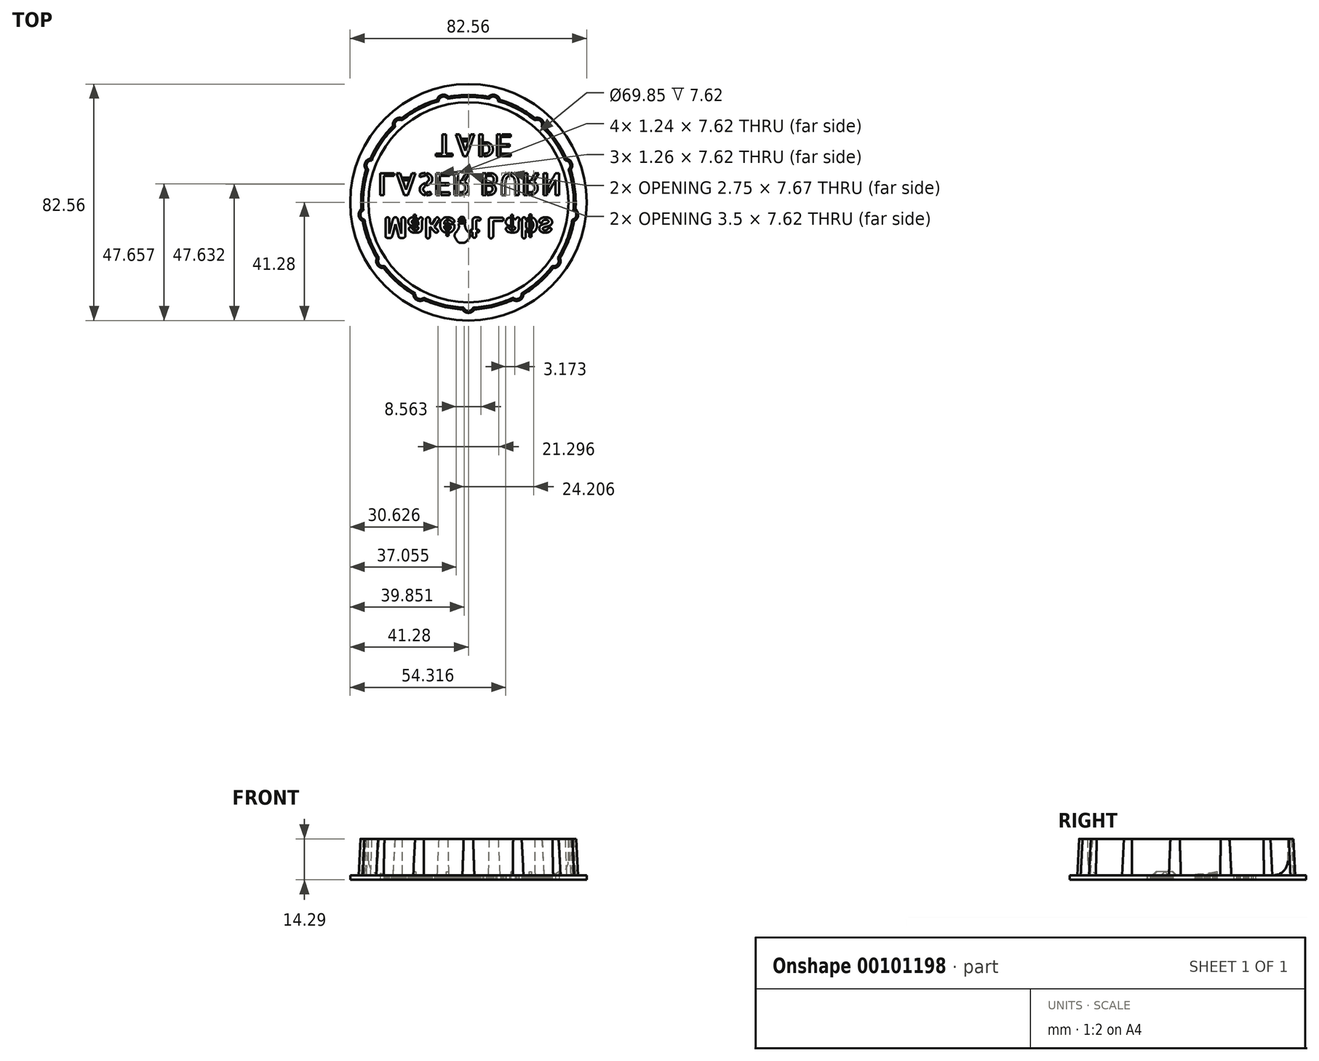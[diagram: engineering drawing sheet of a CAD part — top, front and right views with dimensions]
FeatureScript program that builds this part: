
annotation { "Feature Type Name" : "Feature", "Feature Type Description" : "" }
export const myFeature = defineFeature(function(context is Context, id is Id, definition is map)
    precondition{}
    {
        {
            var Q0;
            Q0=qCreatedBy(makeId("Top.planeOp"),FACE);
            var sketch = newSketch(context, id + "F0", { "sketchPlane" : qUnion([Q0])});
            skCircle(sketch, "E0", {"center": v(0, 0) * mm, "radius": 37.47 * mm});
            skArc(sketch, "E1", {"start": v(-2.08, -37.4) * mm, "mid": v(0, -38.6) * mm, "end": v(2.08, -37.4) * mm});
            skArc(sketch, "E2.1.0", {"start": v(15.54, -34.09) * mm, "mid": v(17.94, -34.19) * mm, "end": v(19.23, -32.16) * mm});
            skArc(sketch, "E2.2.0", {"start": v(29.6, -22.96) * mm, "mid": v(31.77, -21.93) * mm, "end": v(31.97, -19.54) * mm});
            skArc(sketch, "E2.3.0", {"start": v(36.88, -6.57) * mm, "mid": v(38.33, -4.65) * mm, "end": v(37.39, -2.44) * mm});
            skArc(sketch, "E2.4.0", {"start": v(35.71, 11.32) * mm, "mid": v(36.1, 13.7) * mm, "end": v(34.24, 15.2) * mm});
            skArc(sketch, "E2.5.0", {"start": v(26.36, 26.62) * mm, "mid": v(25.6, 28.9) * mm, "end": v(23.25, 29.38) * mm});
            skArc(sketch, "E2.6.0", {"start": v(10.97, 35.82) * mm, "mid": v(9.24, 37.49) * mm, "end": v(6.93, 36.82) * mm});
            skArc(sketch, "E2.7.0", {"start": v(-6.93, 36.82) * mm, "mid": v(-9.24, 37.49) * mm, "end": v(-10.97, 35.82) * mm});
            skArc(sketch, "E2.8.0", {"start": v(-23.25, 29.38) * mm, "mid": v(-25.6, 28.9) * mm, "end": v(-26.36, 26.62) * mm});
            skArc(sketch, "E2.9.0", {"start": v(-34.24, 15.2) * mm, "mid": v(-36.1, 13.7) * mm, "end": v(-35.71, 11.32) * mm});
            skArc(sketch, "E2.10.0", {"start": v(-37.39, -2.44) * mm, "mid": v(-38.33, -4.65) * mm, "end": v(-36.88, -6.57) * mm});
            skArc(sketch, "E2.11.0", {"start": v(-31.97, -19.54) * mm, "mid": v(-31.77, -21.93) * mm, "end": v(-29.6, -22.96) * mm});
            skArc(sketch, "E2.12.0", {"start": v(-19.23, -32.16) * mm, "mid": v(-17.94, -34.19) * mm, "end": v(-15.54, -34.09) * mm});
            skLineSegment(sketch, "E3", {"start": v(-2.08, -37.4) * mm, "end": v(0, -36.2) * mm});
            skLineSegment(sketch, "E4", {"start": v(0, -36.2) * mm, "end": v(2.08, -37.4) * mm});
            skSolve(sketch);
        }
        {
            var Q0;
            Q0 = qSketchRegion(id + "F0", true);
            extrude(context, id + "F1", {"entities" : qUnion([Q0]), "depth" : 12.7 * mm, "hasDraft" : true, "draftAngle" : 3 * degree, "draftPullDirection" : true});
        }
        {
            var Q0;
            Q0=qCreatedBy(makeId("Top.planeOp"),FACE);
            var sketch = newSketch(context, id + "F2", { "sketchPlane" : qUnion([Q0])});
            skCircle(sketch, "E5", {"center": v(0, 0) * mm, "radius": 38.1 * mm, "construction": true});
            skCircle(sketch, "E6", {"center": v(0, 0) * mm, "radius": 41.28 * mm});
            skSolve(sketch);
        }
        {
            var Q0;
            Q0 = qSketchRegion(id + "F2", true);
            extrude(context, id + "F3", {"entities" : qUnion([Q0]), "operationType" : NewBodyOperationType.ADD, "oppositeDirection" : true, "depth" : 1.59 * mm});
        }
        {
            var Q0;
            Q0=makeQuery(id+"F1.opExtrude","CAP_FACE",FACE,{"disambiguationData":[OSD([sQuery(id+"F0.wireOp",EDGE,"E0"),sQuery(id+"F0.wireOp",EDGE,"E1"),sQuery(id+"F0.wireOp",EDGE,"E2.1.0"),sQuery(id+"F0.wireOp",EDGE,"E2.2.0"),sQuery(id+"F0.wireOp",EDGE,"E2.3.0"),sQuery(id+"F0.wireOp",EDGE,"E2.4.0"),sQuery(id+"F0.wireOp",EDGE,"E2.5.0"),sQuery(id+"F0.wireOp",EDGE,"E2.6.0"),sQuery(id+"F0.wireOp",EDGE,"E2.7.0"),sQuery(id+"F0.wireOp",EDGE,"E2.8.0"),sQuery(id+"F0.wireOp",EDGE,"E2.9.0"),sQuery(id+"F0.wireOp",EDGE,"E2.10.0"),sQuery(id+"F0.wireOp",EDGE,"E2.11.0"),sQuery(id+"F0.wireOp",EDGE,"E2.12.0")])],"isStart":false});
            var sketch = newSketch(context, id + "F4", { "sketchPlane" : qUnion([Q0])});
            skCircle(sketch, "E7", {"center": v(0, 0) * mm, "radius": 34.93 * mm});
            skSolve(sketch);
        }
        {
            var Q0;
            Q0 = qSketchRegion(id + "F4", true);
            extrude(context, id + "F5", {"entities" : qUnion([Q0]), "operationType" : NewBodyOperationType.REMOVE, "oppositeDirection" : true, "depth" : 12.7 * mm});
        }
        {
            var Q0;
            Q0=makeQuery(id+"F5.boolean.opBoolean","COPY",EDGE,{"derivedFrom":makeQuery(id+"F5.opExtrude","CAP_EDGE",EDGE,{"disambiguationData":[OSD([sQuery(id+"F4.wireOp",EDGE,"E7")])],"isStart":false})});
            fillet(context, id + "F6", {"entities" : qUnion([Q0]), "radius" : 5.08 * mm, "tangentPropagation" : true, "allowEdgeOverflow" : false});
        }
        {
            var Q0;
            Q0=makeQuery(id+"F3.opExtrude","CAP_FACE",FACE,{"disambiguationData":[OSD([sQuery(id+"F2.wireOp",EDGE,"E6")])],"isStart":false});
            var sketch = newSketch(context, id + "F7", { "sketchPlane" : qUnion([Q0])});
            skFitSpline(sketch, "E8", {"points": [v(-27.6, 6.08) * mm, v(-27.6, 5.8) * mm, v(-27.65, 5.6) * mm, v(-27.77, 5.47) * mm]});
            skFitSpline(sketch, "E9", {"points": [v(-27.77, 5.47) * mm, v(-27.9, 5.34) * mm, v(-28.05, 5.27) * mm, v(-28.25, 5.27) * mm]});
            skFitSpline(sketch, "E10", {"points": [v(-28.25, 5.27) * mm, v(-28.44, 5.27) * mm, v(-28.6, 5.34) * mm, v(-28.72, 5.47) * mm]});
            skFitSpline(sketch, "E11", {"points": [v(-28.72, 5.47) * mm, v(-28.84, 5.6) * mm, v(-28.9, 5.8) * mm, v(-28.9, 6.08) * mm]});
            skLineSegment(sketch, "E12", {"start": v(-26.46, 6.45) * mm, "end": v(-27.6, 10.95) * mm});
            skLineSegment(sketch, "E13", {"start": v(-27.6, 10.95) * mm, "end": v(-27.6, 6.08) * mm});
            skFitSpline(sketch, "E14", {"points": [v(-28.9, 11.66) * mm, v(-28.9, 11.97) * mm, v(-28.83, 12.18) * mm, v(-28.66, 12.28) * mm]});
            skFitSpline(sketch, "E15", {"points": [v(-28.66, 12.28) * mm, v(-28.5, 12.4) * mm, v(-28.29, 12.45) * mm, v(-28.02, 12.45) * mm]});
            skLineSegment(sketch, "E16", {"start": v(-28.9, 6.08) * mm, "end": v(-28.9, 11.66) * mm});
            skLineSegment(sketch, "E17", {"start": v(-28.9, 11.66) * mm, "end": v(-28.9, 6.08) * mm});
            skFitSpline(sketch, "E18", {"points": [v(-27.57, 12.45) * mm, v(-27.3, 12.45) * mm, v(-27.11, 12.42) * mm, v(-27, 12.37) * mm]});
            skFitSpline(sketch, "E19", {"points": [v(-27, 12.37) * mm, v(-26.87, 12.33) * mm, v(-26.78, 12.24) * mm, v(-26.73, 12.11) * mm]});
            skFitSpline(sketch, "E20", {"points": [v(-26.73, 12.11) * mm, v(-26.67, 11.99) * mm, v(-26.6, 11.78) * mm, v(-26.53, 11.5) * mm]});
            skLineSegment(sketch, "E21", {"start": v(-28.02, 12.45) * mm, "end": v(-27.57, 12.45) * mm});
            skLineSegment(sketch, "E22", {"start": v(-27.57, 12.45) * mm, "end": v(-28.02, 12.45) * mm});
            skFitSpline(sketch, "E23", {"points": [v(-24.48, 11.5) * mm, v(-24.4, 11.78) * mm, v(-24.34, 11.99) * mm, v(-24.28, 12.11) * mm]});
            skFitSpline(sketch, "E24", {"points": [v(-24.28, 12.11) * mm, v(-24.22, 12.24) * mm, v(-24.13, 12.33) * mm, v(-24.01, 12.37) * mm]});
            skFitSpline(sketch, "E25", {"points": [v(-24.01, 12.37) * mm, v(-23.9, 12.42) * mm, v(-23.7, 12.45) * mm, v(-23.43, 12.45) * mm]});
            skLineSegment(sketch, "E26", {"start": v(-26.53, 11.5) * mm, "end": v(-25.5, 7.64) * mm});
            skLineSegment(sketch, "E27", {"start": v(-25.5, 7.64) * mm, "end": v(-24.48, 11.5) * mm});
            skFitSpline(sketch, "E28", {"points": [v(-23, 12.45) * mm, v(-22.72, 12.45) * mm, v(-22.5, 12.4) * mm, v(-22.34, 12.28) * mm]});
            skFitSpline(sketch, "E29", {"points": [v(-22.34, 12.28) * mm, v(-22.18, 12.18) * mm, v(-22.1, 11.97) * mm, v(-22.1, 11.66) * mm]});
            skLineSegment(sketch, "E30", {"start": v(-23.43, 12.45) * mm, "end": v(-23, 12.45) * mm});
            skLineSegment(sketch, "E31", {"start": v(-23, 12.45) * mm, "end": v(-23.43, 12.45) * mm});
            skFitSpline(sketch, "E32", {"points": [v(-22.1, 6.08) * mm, v(-22.1, 5.8) * mm, v(-22.16, 5.6) * mm, v(-22.28, 5.47) * mm]});
            skFitSpline(sketch, "E33", {"points": [v(-22.28, 5.47) * mm, v(-22.4, 5.34) * mm, v(-22.56, 5.27) * mm, v(-22.77, 5.27) * mm]});
            skFitSpline(sketch, "E34", {"points": [v(-22.77, 5.27) * mm, v(-22.95, 5.27) * mm, v(-23.11, 5.34) * mm, v(-23.23, 5.47) * mm]});
            skFitSpline(sketch, "E35", {"points": [v(-23.23, 5.47) * mm, v(-23.35, 5.6) * mm, v(-23.41, 5.8) * mm, v(-23.41, 6.08) * mm]});
            skLineSegment(sketch, "E36", {"start": v(-22.1, 11.66) * mm, "end": v(-22.1, 6.08) * mm});
            skLineSegment(sketch, "E37", {"start": v(-22.1, 6.08) * mm, "end": v(-22.1, 11.66) * mm});
            skFitSpline(sketch, "E38", {"points": [v(-24.55, 6.45) * mm, v(-24.62, 6.16) * mm, v(-24.68, 5.95) * mm, v(-24.73, 5.81) * mm]});
            skFitSpline(sketch, "E39", {"points": [v(-24.73, 5.81) * mm, v(-24.77, 5.68) * mm, v(-24.86, 5.55) * mm, v(-24.98, 5.44) * mm]});
            skFitSpline(sketch, "E40", {"points": [v(-24.98, 5.44) * mm, v(-25.1, 5.33) * mm, v(-25.28, 5.27) * mm, v(-25.5, 5.27) * mm]});
            skFitSpline(sketch, "E41", {"points": [v(-25.5, 5.27) * mm, v(-25.67, 5.27) * mm, v(-25.81, 5.3) * mm, v(-25.93, 5.38) * mm]});
            skFitSpline(sketch, "E42", {"points": [v(-25.93, 5.38) * mm, v(-26.04, 5.45) * mm, v(-26.13, 5.54) * mm, v(-26.2, 5.66) * mm]});
            skFitSpline(sketch, "E43", {"points": [v(-26.2, 5.66) * mm, v(-26.26, 5.77) * mm, v(-26.31, 5.9) * mm, v(-26.35, 6.03) * mm]});
            skFitSpline(sketch, "E44", {"points": [v(-26.35, 6.03) * mm, v(-26.38, 6.17) * mm, v(-26.42, 6.3) * mm, v(-26.46, 6.45) * mm]});
            skLineSegment(sketch, "E45", {"start": v(-23.41, 6.08) * mm, "end": v(-23.41, 10.95) * mm});
            skLineSegment(sketch, "E46", {"start": v(-23.41, 10.95) * mm, "end": v(-24.55, 6.45) * mm});
            skFitSpline(sketch, "E47", {"points": [v(-17.4, 6.01) * mm, v(-17.72, 5.76) * mm, v(-18.03, 5.58) * mm, v(-18.33, 5.46) * mm]});
            skFitSpline(sketch, "E48", {"points": [v(-18.33, 5.46) * mm, v(-18.62, 5.33) * mm, v(-18.96, 5.27) * mm, v(-19.32, 5.27) * mm]});
            skFitSpline(sketch, "E49", {"points": [v(-19.32, 5.27) * mm, v(-19.66, 5.27) * mm, v(-19.96, 5.34) * mm, v(-20.21, 5.47) * mm]});
            skFitSpline(sketch, "E50", {"points": [v(-20.21, 5.47) * mm, v(-20.47, 5.6) * mm, v(-20.66, 5.78) * mm, v(-20.8, 6.01) * mm]});
            skFitSpline(sketch, "E51", {"points": [v(-20.8, 6.01) * mm, v(-20.94, 6.24) * mm, v(-21, 6.49) * mm, v(-21, 6.75) * mm]});
            skFitSpline(sketch, "E52", {"points": [v(-21, 6.75) * mm, v(-21, 7.11) * mm, v(-20.9, 7.42) * mm, v(-20.67, 7.67) * mm]});
            skFitSpline(sketch, "E53", {"points": [v(-20.67, 7.67) * mm, v(-20.44, 7.93) * mm, v(-20.13, 8.1) * mm, v(-19.73, 8.18) * mm]});
            skFitSpline(sketch, "E54", {"points": [v(-19.73, 8.18) * mm, v(-19.65, 8.2) * mm, v(-19.44, 8.24) * mm, v(-19.1, 8.31) * mm]});
            skFitSpline(sketch, "E55", {"points": [v(-19.1, 8.31) * mm, v(-18.78, 8.38) * mm, v(-18.5, 8.44) * mm, v(-18.26, 8.5) * mm]});
            skFitSpline(sketch, "E56", {"points": [v(-18.26, 8.5) * mm, v(-18.02, 8.55) * mm, v(-17.77, 8.62) * mm, v(-17.5, 8.7) * mm]});
            skFitSpline(sketch, "E57", {"points": [v(-17.5, 8.7) * mm, v(-17.5, 9.05) * mm, v(-17.58, 9.3) * mm, v(-17.7, 9.46) * mm]});
            skFitSpline(sketch, "E58", {"points": [v(-17.7, 9.46) * mm, v(-17.82, 9.63) * mm, v(-18.08, 9.7) * mm, v(-18.47, 9.7) * mm]});
            skFitSpline(sketch, "E59", {"points": [v(-18.47, 9.7) * mm, v(-18.8, 9.7) * mm, v(-19.05, 9.66) * mm, v(-19.22, 9.57) * mm]});
            skFitSpline(sketch, "E60", {"points": [v(-19.22, 9.57) * mm, v(-19.39, 9.47) * mm, v(-19.53, 9.34) * mm, v(-19.65, 9.15) * mm]});
            skFitSpline(sketch, "E61", {"points": [v(-19.65, 9.15) * mm, v(-19.77, 8.96) * mm, v(-19.86, 8.84) * mm, v(-19.9, 8.78) * mm]});
            skFitSpline(sketch, "E62", {"points": [v(-19.9, 8.78) * mm, v(-19.96, 8.72) * mm, v(-20.07, 8.7) * mm, v(-20.23, 8.7) * mm]});
            skFitSpline(sketch, "E63", {"points": [v(-20.23, 8.7) * mm, v(-20.38, 8.7) * mm, v(-20.5, 8.74) * mm, v(-20.61, 8.83) * mm]});
            skFitSpline(sketch, "E64", {"points": [v(-20.61, 8.83) * mm, v(-20.72, 8.93) * mm, v(-20.77, 9.05) * mm, v(-20.77, 9.2) * mm]});
            skFitSpline(sketch, "E65", {"points": [v(-20.77, 9.2) * mm, v(-20.77, 9.43) * mm, v(-20.7, 9.65) * mm, v(-20.53, 9.87) * mm]});
            skFitSpline(sketch, "E66", {"points": [v(-20.53, 9.87) * mm, v(-20.36, 10.09) * mm, v(-20.1, 10.27) * mm, v(-19.76, 10.4) * mm]});
            skFitSpline(sketch, "E67", {"points": [v(-19.76, 10.4) * mm, v(-19.42, 10.55) * mm, v(-18.98, 10.62) * mm, v(-18.47, 10.62) * mm]});
            skFitSpline(sketch, "E68", {"points": [v(-18.47, 10.62) * mm, v(-17.9, 10.62) * mm, v(-17.44, 10.55) * mm, v(-17.1, 10.42) * mm]});
            skFitSpline(sketch, "E69", {"points": [v(-17.1, 10.42) * mm, v(-16.78, 10.28) * mm, v(-16.54, 10.07) * mm, v(-16.4, 9.77) * mm]});
            skFitSpline(sketch, "E70", {"points": [v(-16.4, 9.77) * mm, v(-16.27, 9.47) * mm, v(-16.2, 9.08) * mm, v(-16.2, 8.6) * mm]});
            skFitSpline(sketch, "E71", {"points": [v(-16.2, 8.6) * mm, v(-16.2, 8.29) * mm, v(-16.2, 8.03) * mm, v(-16.2, 7.81) * mm]});
            skFitSpline(sketch, "E72", {"points": [v(-16.2, 7.81) * mm, v(-16.2, 7.6) * mm, v(-16.2, 7.36) * mm, v(-16.21, 7.1) * mm]});
            skFitSpline(sketch, "E73", {"points": [v(-16.21, 7.1) * mm, v(-16.21, 6.85) * mm, v(-16.17, 6.6) * mm, v(-16.09, 6.32) * mm]});
            skFitSpline(sketch, "E74", {"points": [v(-16.09, 6.32) * mm, v(-16, 6.05) * mm, v(-15.97, 5.88) * mm, v(-15.97, 5.8) * mm]});
            skFitSpline(sketch, "E75", {"points": [v(-15.97, 5.8) * mm, v(-15.97, 5.67) * mm, v(-16.03, 5.55) * mm, v(-16.16, 5.44) * mm]});
            skFitSpline(sketch, "E76", {"points": [v(-16.16, 5.44) * mm, v(-16.28, 5.33) * mm, v(-16.43, 5.27) * mm, v(-16.59, 5.27) * mm]});
            skFitSpline(sketch, "E77", {"points": [v(-16.59, 5.27) * mm, v(-16.72, 5.27) * mm, v(-16.85, 5.33) * mm, v(-16.99, 5.46) * mm]});
            skFitSpline(sketch, "E78", {"points": [v(-16.99, 5.46) * mm, v(-17.12, 5.59) * mm, v(-17.26, 5.77) * mm, v(-17.4, 6.01) * mm]});
            skFitSpline(sketch, "E79", {"points": [v(-17.5, 7.91) * mm, v(-17.68, 7.84) * mm, v(-17.96, 7.77) * mm, v(-18.33, 7.69) * mm]});
            skFitSpline(sketch, "E80", {"points": [v(-18.33, 7.69) * mm, v(-18.7, 7.61) * mm, v(-18.95, 7.55) * mm, v(-19.1, 7.52) * mm]});
            skFitSpline(sketch, "E81", {"points": [v(-19.1, 7.52) * mm, v(-19.23, 7.48) * mm, v(-19.37, 7.4) * mm, v(-19.5, 7.3) * mm]});
            skFitSpline(sketch, "E82", {"points": [v(-19.5, 7.3) * mm, v(-19.63, 7.2) * mm, v(-19.7, 7.04) * mm, v(-19.7, 6.85) * mm]});
            skFitSpline(sketch, "E83", {"points": [v(-19.7, 6.85) * mm, v(-19.7, 6.65) * mm, v(-19.62, 6.48) * mm, v(-19.46, 6.34) * mm]});
            skFitSpline(sketch, "E84", {"points": [v(-19.46, 6.34) * mm, v(-19.31, 6.2) * mm, v(-19.12, 6.13) * mm, v(-18.87, 6.13) * mm]});
            skFitSpline(sketch, "E85", {"points": [v(-18.87, 6.13) * mm, v(-18.61, 6.13) * mm, v(-18.37, 6.19) * mm, v(-18.15, 6.3) * mm]});
            skFitSpline(sketch, "E86", {"points": [v(-18.15, 6.3) * mm, v(-17.93, 6.42) * mm, v(-17.77, 6.56) * mm, v(-17.67, 6.74) * mm]});
            skFitSpline(sketch, "E87", {"points": [v(-17.67, 6.74) * mm, v(-17.55, 6.94) * mm, v(-17.5, 7.27) * mm, v(-17.5, 7.73) * mm]});
            skLineSegment(sketch, "E88", {"start": v(-17.5, 7.73) * mm, "end": v(-17.5, 7.91) * mm});
            skLineSegment(sketch, "E89", {"start": v(-17.5, 7.91) * mm, "end": v(-17.5, 7.91) * mm});
            skLineSegment(sketch, "E90", {"start": v(-17.5, 7.91) * mm, "end": v(-17.5, 7.73) * mm});
            skFitSpline(sketch, "E91", {"points": [v(-13.47, 6.06) * mm, v(-13.47, 5.8) * mm, v(-13.54, 5.61) * mm, v(-13.67, 5.48) * mm]});
            skFitSpline(sketch, "E92", {"points": [v(-13.67, 5.48) * mm, v(-13.8, 5.34) * mm, v(-13.95, 5.27) * mm, v(-14.13, 5.27) * mm]});
            skFitSpline(sketch, "E93", {"points": [v(-14.13, 5.27) * mm, v(-14.33, 5.27) * mm, v(-14.49, 5.34) * mm, v(-14.6, 5.47) * mm]});
            skFitSpline(sketch, "E94", {"points": [v(-14.6, 5.47) * mm, v(-14.72, 5.6) * mm, v(-14.78, 5.8) * mm, v(-14.78, 6.07) * mm]});
            skLineSegment(sketch, "E95", {"start": v(-11.6, 5.87) * mm, "end": v(-12.76, 7.78) * mm});
            skLineSegment(sketch, "E96", {"start": v(-12.76, 7.78) * mm, "end": v(-13.47, 7.1) * mm});
            skLineSegment(sketch, "E97", {"start": v(-13.47, 7.1) * mm, "end": v(-13.47, 6.06) * mm});
            skFitSpline(sketch, "E98", {"points": [v(-14.78, 11.67) * mm, v(-14.78, 11.96) * mm, v(-14.72, 12.18) * mm, v(-14.6, 12.34) * mm]});
            skFitSpline(sketch, "E99", {"points": [v(-14.6, 12.34) * mm, v(-14.5, 12.49) * mm, v(-14.34, 12.57) * mm, v(-14.13, 12.57) * mm]});
            skFitSpline(sketch, "E100", {"points": [v(-14.13, 12.57) * mm, v(-13.93, 12.57) * mm, v(-13.77, 12.5) * mm, v(-13.65, 12.36) * mm]});
            skFitSpline(sketch, "E101", {"points": [v(-13.65, 12.36) * mm, v(-13.53, 12.22) * mm, v(-13.47, 12.02) * mm, v(-13.47, 11.75) * mm]});
            skLineSegment(sketch, "E102", {"start": v(-14.78, 6.07) * mm, "end": v(-14.78, 11.67) * mm});
            skLineSegment(sketch, "E103", {"start": v(-14.78, 11.67) * mm, "end": v(-14.78, 6.07) * mm});
            skFitSpline(sketch, "E104", {"points": [v(-12, 10.11) * mm, v(-11.8, 10.3) * mm, v(-11.67, 10.44) * mm, v(-11.57, 10.5) * mm]});
            skFitSpline(sketch, "E105", {"points": [v(-11.57, 10.5) * mm, v(-11.48, 10.58) * mm, v(-11.36, 10.61) * mm, v(-11.22, 10.61) * mm]});
            skFitSpline(sketch, "E106", {"points": [v(-11.22, 10.61) * mm, v(-11.06, 10.61) * mm, v(-10.92, 10.56) * mm, v(-10.81, 10.46) * mm]});
            skFitSpline(sketch, "E107", {"points": [v(-10.81, 10.46) * mm, v(-10.7, 10.35) * mm, v(-10.65, 10.22) * mm, v(-10.65, 10.06) * mm]});
            skFitSpline(sketch, "E108", {"points": [v(-10.65, 10.06) * mm, v(-10.65, 9.87) * mm, v(-10.83, 9.61) * mm, v(-11.18, 9.3) * mm]});
            skLineSegment(sketch, "E109", {"start": v(-13.47, 11.75) * mm, "end": v(-13.47, 8.56) * mm});
            skLineSegment(sketch, "E110", {"start": v(-13.47, 8.56) * mm, "end": v(-12, 10.11) * mm});
            skFitSpline(sketch, "E111", {"points": [v(-10.53, 6.54) * mm, v(-10.43, 6.38) * mm, v(-10.36, 6.26) * mm, v(-10.32, 6.18) * mm]});
            skFitSpline(sketch, "E112", {"points": [v(-10.32, 6.18) * mm, v(-10.28, 6.1) * mm, v(-10.25, 6.02) * mm, v(-10.25, 5.94) * mm]});
            skFitSpline(sketch, "E113", {"points": [v(-10.25, 5.94) * mm, v(-10.25, 5.74) * mm, v(-10.31, 5.57) * mm, v(-10.42, 5.45) * mm]});
            skFitSpline(sketch, "E114", {"points": [v(-10.42, 5.45) * mm, v(-10.54, 5.33) * mm, v(-10.69, 5.27) * mm, v(-10.87, 5.27) * mm]});
            skFitSpline(sketch, "E115", {"points": [v(-10.87, 5.27) * mm, v(-11.04, 5.27) * mm, v(-11.16, 5.31) * mm, v(-11.25, 5.4) * mm]});
            skFitSpline(sketch, "E116", {"points": [v(-11.25, 5.4) * mm, v(-11.33, 5.49) * mm, v(-11.45, 5.64) * mm, v(-11.6, 5.87) * mm]});
            skLineSegment(sketch, "E117", {"start": v(-11.18, 9.3) * mm, "end": v(-11.88, 8.65) * mm});
            skLineSegment(sketch, "E118", {"start": v(-11.88, 8.65) * mm, "end": v(-10.53, 6.54) * mm});
            skFitSpline(sketch, "E119", {"points": [v(-8.5, 7.62) * mm, v(-8.5, 7.32) * mm, v(-8.43, 7.06) * mm, v(-8.32, 6.83) * mm]});
            skFitSpline(sketch, "E120", {"points": [v(-8.32, 6.83) * mm, v(-8.2, 6.6) * mm, v(-8.04, 6.43) * mm, v(-7.85, 6.32) * mm]});
            skFitSpline(sketch, "E121", {"points": [v(-7.85, 6.32) * mm, v(-7.66, 6.2) * mm, v(-7.44, 6.14) * mm, v(-7.2, 6.14) * mm]});
            skFitSpline(sketch, "E122", {"points": [v(-7.2, 6.14) * mm, v(-7.05, 6.14) * mm, v(-6.9, 6.16) * mm, v(-6.78, 6.2) * mm]});
            skFitSpline(sketch, "E123", {"points": [v(-6.78, 6.2) * mm, v(-6.65, 6.23) * mm, v(-6.52, 6.3) * mm, v(-6.4, 6.37) * mm]});
            skFitSpline(sketch, "E124", {"points": [v(-6.4, 6.37) * mm, v(-6.28, 6.45) * mm, v(-6.17, 6.53) * mm, v(-6.06, 6.62) * mm]});
            skFitSpline(sketch, "E125", {"points": [v(-6.06, 6.62) * mm, v(-5.96, 6.71) * mm, v(-5.83, 6.83) * mm, v(-5.66, 6.99) * mm]});
            skFitSpline(sketch, "E126", {"points": [v(-5.66, 6.99) * mm, v(-5.6, 7.05) * mm, v(-5.5, 7.08) * mm, v(-5.38, 7.08) * mm]});
            skFitSpline(sketch, "E127", {"points": [v(-5.38, 7.08) * mm, v(-5.24, 7.08) * mm, v(-5.13, 7.04) * mm, v(-5.05, 6.96) * mm]});
            skFitSpline(sketch, "E128", {"points": [v(-5.05, 6.96) * mm, v(-4.96, 6.9) * mm, v(-4.92, 6.79) * mm, v(-4.92, 6.65) * mm]});
            skFitSpline(sketch, "E129", {"points": [v(-4.92, 6.65) * mm, v(-4.92, 6.53) * mm, v(-4.97, 6.4) * mm, v(-5.06, 6.24) * mm]});
            skFitSpline(sketch, "E130", {"points": [v(-5.06, 6.24) * mm, v(-5.16, 6.08) * mm, v(-5.3, 5.92) * mm, v(-5.48, 5.78) * mm]});
            skFitSpline(sketch, "E131", {"points": [v(-5.48, 5.78) * mm, v(-5.67, 5.63) * mm, v(-5.9, 5.51) * mm, v(-6.2, 5.42) * mm]});
            skFitSpline(sketch, "E132", {"points": [v(-6.2, 5.42) * mm, v(-6.47, 5.32) * mm, v(-6.8, 5.27) * mm, v(-7.17, 5.27) * mm]});
            skFitSpline(sketch, "E133", {"points": [v(-7.17, 5.27) * mm, v(-8.01, 5.27) * mm, v(-8.67, 5.51) * mm, v(-9.14, 6) * mm]});
            skFitSpline(sketch, "E134", {"points": [v(-9.14, 6) * mm, v(-9.6, 6.47) * mm, v(-9.84, 7.13) * mm, v(-9.84, 7.95) * mm]});
            skFitSpline(sketch, "E135", {"points": [v(-9.84, 7.95) * mm, v(-9.84, 8.34) * mm, v(-9.78, 8.7) * mm, v(-9.67, 9.03) * mm]});
            skFitSpline(sketch, "E136", {"points": [v(-9.67, 9.03) * mm, v(-9.55, 9.36) * mm, v(-9.38, 9.65) * mm, v(-9.16, 9.89) * mm]});
            skFitSpline(sketch, "E137", {"points": [v(-9.16, 9.89) * mm, v(-8.94, 10.12) * mm, v(-8.67, 10.3) * mm, v(-8.34, 10.43) * mm]});
            skFitSpline(sketch, "E138", {"points": [v(-8.34, 10.43) * mm, v(-8.02, 10.56) * mm, v(-7.66, 10.62) * mm, v(-7.27, 10.62) * mm]});
            skFitSpline(sketch, "E139", {"points": [v(-7.27, 10.62) * mm, v(-6.75, 10.62) * mm, v(-6.31, 10.51) * mm, v(-5.95, 10.3) * mm]});
            skFitSpline(sketch, "E140", {"points": [v(-5.95, 10.3) * mm, v(-5.58, 10.08) * mm, v(-5.3, 9.8) * mm, v(-5.12, 9.46) * mm]});
            skFitSpline(sketch, "E141", {"points": [v(-5.12, 9.46) * mm, v(-4.94, 9.11) * mm, v(-4.85, 8.76) * mm, v(-4.85, 8.4) * mm]});
            skFitSpline(sketch, "E142", {"points": [v(-4.85, 8.4) * mm, v(-4.85, 8.08) * mm, v(-4.94, 7.86) * mm, v(-5.13, 7.77) * mm]});
            skFitSpline(sketch, "E143", {"points": [v(-5.13, 7.77) * mm, v(-5.32, 7.67) * mm, v(-5.59, 7.62) * mm, v(-5.93, 7.62) * mm]});
            skLineSegment(sketch, "E144", {"start": v(-5.93, 7.62) * mm, "end": v(-8.5, 7.62) * mm});
            skLineSegment(sketch, "E145", {"start": v(-8.5, 7.62) * mm, "end": v(-5.93, 7.62) * mm});
            skFitSpline(sketch, "E146", {"points": [v(-6.12, 8.37) * mm, v(-6.15, 8.81) * mm, v(-6.27, 9.15) * mm, v(-6.48, 9.37) * mm]});
            skFitSpline(sketch, "E147", {"points": [v(-6.48, 9.37) * mm, v(-6.69, 9.6) * mm, v(-6.97, 9.7) * mm, v(-7.3, 9.7) * mm]});
            skFitSpline(sketch, "E148", {"points": [v(-7.3, 9.7) * mm, v(-7.64, 9.7) * mm, v(-7.9, 9.6) * mm, v(-8.12, 9.37) * mm]});
            skFitSpline(sketch, "E149", {"points": [v(-8.12, 9.37) * mm, v(-8.33, 9.14) * mm, v(-8.45, 8.8) * mm, v(-8.5, 8.37) * mm]});
            skLineSegment(sketch, "E150", {"start": v(-8.5, 8.37) * mm, "end": v(-6.12, 8.37) * mm});
            skLineSegment(sketch, "E151", {"start": v(-6.12, 8.37) * mm, "end": v(-8.5, 8.37) * mm});
            skFitSpline(sketch, "E152", {"points": [v(1.4, 11.29) * mm, v(1.4, 11.5) * mm, v(1.41, 11.66) * mm, v(1.42, 11.78) * mm]});
            skFitSpline(sketch, "E153", {"points": [v(1.42, 11.78) * mm, v(1.43, 11.9) * mm, v(1.46, 12) * mm, v(1.52, 12.1) * mm]});
            skFitSpline(sketch, "E154", {"points": [v(1.52, 12.1) * mm, v(1.57, 12.18) * mm, v(1.64, 12.26) * mm, v(1.74, 12.31) * mm]});
            skFitSpline(sketch, "E155", {"points": [v(1.74, 12.31) * mm, v(1.83, 12.37) * mm, v(1.94, 12.4) * mm, v(2.06, 12.4) * mm]});
            skFitSpline(sketch, "E156", {"points": [v(2.06, 12.4) * mm, v(2.23, 12.4) * mm, v(2.38, 12.33) * mm, v(2.51, 12.2) * mm]});
            skFitSpline(sketch, "E157", {"points": [v(2.51, 12.2) * mm, v(2.6, 12.13) * mm, v(2.66, 12.02) * mm, v(2.68, 11.9) * mm]});
            skFitSpline(sketch, "E158", {"points": [v(2.68, 11.9) * mm, v(2.7, 11.78) * mm, v(2.72, 11.61) * mm, v(2.72, 11.4) * mm]});
            skLineSegment(sketch, "E159", {"start": v(1.26, 10.5) * mm, "end": v(1.4, 10.5) * mm});
            skLineSegment(sketch, "E160", {"start": v(1.4, 10.5) * mm, "end": v(1.4, 11.29) * mm});
            skFitSpline(sketch, "E161", {"points": [v(3.2, 10.5) * mm, v(3.39, 10.5) * mm, v(3.53, 10.45) * mm, v(3.63, 10.36) * mm]});
            skFitSpline(sketch, "E162", {"points": [v(3.63, 10.36) * mm, v(3.72, 10.28) * mm, v(3.77, 10.16) * mm, v(3.77, 10.03) * mm]});
            skFitSpline(sketch, "E163", {"points": [v(3.77, 10.03) * mm, v(3.77, 9.85) * mm, v(3.7, 9.73) * mm, v(3.56, 9.65) * mm]});
            skFitSpline(sketch, "E164", {"points": [v(3.56, 9.65) * mm, v(3.42, 9.58) * mm, v(3.22, 9.55) * mm, v(2.96, 9.55) * mm]});
            skLineSegment(sketch, "E165", {"start": v(2.72, 11.4) * mm, "end": v(2.72, 10.5) * mm});
            skLineSegment(sketch, "E166", {"start": v(2.72, 10.5) * mm, "end": v(3.2, 10.5) * mm});
            skFitSpline(sketch, "E167", {"points": [v(2.72, 7.13) * mm, v(2.72, 6.93) * mm, v(2.73, 6.77) * mm, v(2.74, 6.66) * mm]});
            skFitSpline(sketch, "E168", {"points": [v(2.74, 6.66) * mm, v(2.75, 6.55) * mm, v(2.8, 6.46) * mm, v(2.86, 6.39) * mm]});
            skFitSpline(sketch, "E169", {"points": [v(2.86, 6.39) * mm, v(2.92, 6.32) * mm, v(3.02, 6.29) * mm, v(3.16, 6.29) * mm]});
            skFitSpline(sketch, "E170", {"points": [v(3.16, 6.29) * mm, v(3.24, 6.29) * mm, v(3.34, 6.3) * mm, v(3.47, 6.33) * mm]});
            skFitSpline(sketch, "E171", {"points": [v(3.47, 6.33) * mm, v(3.6, 6.35) * mm, v(3.7, 6.37) * mm, v(3.78, 6.37) * mm]});
            skFitSpline(sketch, "E172", {"points": [v(3.78, 6.37) * mm, v(3.89, 6.37) * mm, v(3.98, 6.33) * mm, v(4.07, 6.24) * mm]});
            skFitSpline(sketch, "E173", {"points": [v(4.07, 6.24) * mm, v(4.15, 6.16) * mm, v(4.2, 6.05) * mm, v(4.2, 5.93) * mm]});
            skFitSpline(sketch, "E174", {"points": [v(4.2, 5.93) * mm, v(4.2, 5.71) * mm, v(4.08, 5.55) * mm, v(3.85, 5.44) * mm]});
            skFitSpline(sketch, "E175", {"points": [v(3.85, 5.44) * mm, v(3.62, 5.33) * mm, v(3.29, 5.27) * mm, v(2.85, 5.27) * mm]});
            skFitSpline(sketch, "E176", {"points": [v(2.85, 5.27) * mm, v(2.44, 5.27) * mm, v(2.13, 5.34) * mm, v(1.92, 5.48) * mm]});
            skFitSpline(sketch, "E177", {"points": [v(1.92, 5.48) * mm, v(1.7, 5.62) * mm, v(1.57, 5.8) * mm, v(1.5, 6.05) * mm]});
            skFitSpline(sketch, "E178", {"points": [v(1.5, 6.05) * mm, v(1.44, 6.3) * mm, v(1.4, 6.62) * mm, v(1.4, 7.03) * mm]});
            skLineSegment(sketch, "E179", {"start": v(2.96, 9.55) * mm, "end": v(2.72, 9.55) * mm});
            skLineSegment(sketch, "E180", {"start": v(2.72, 9.55) * mm, "end": v(2.72, 7.13) * mm});
            skFitSpline(sketch, "E181", {"points": [v(1.23, 9.55) * mm, v(1.04, 9.55) * mm, v(0.9, 9.6) * mm, v(0.8, 9.68) * mm]});
            skFitSpline(sketch, "E182", {"points": [v(0.8, 9.68) * mm, v(0.7, 9.77) * mm, v(0.65, 9.89) * mm, v(0.65, 10.03) * mm]});
            skFitSpline(sketch, "E183", {"points": [v(0.65, 10.03) * mm, v(0.65, 10.16) * mm, v(0.7, 10.28) * mm, v(0.8, 10.36) * mm]});
            skFitSpline(sketch, "E184", {"points": [v(0.8, 10.36) * mm, v(0.91, 10.45) * mm, v(1.06, 10.5) * mm, v(1.26, 10.5) * mm]});
            skLineSegment(sketch, "E185", {"start": v(1.4, 7.03) * mm, "end": v(1.4, 9.55) * mm});
            skLineSegment(sketch, "E186", {"start": v(1.4, 9.55) * mm, "end": v(1.23, 9.55) * mm});
            skFitSpline(sketch, "E187", {"points": [v(11.53, 6.57) * mm, v(11.76, 6.57) * mm, v(11.94, 6.5) * mm, v(12.06, 6.4) * mm]});
            skFitSpline(sketch, "E188", {"points": [v(12.06, 6.4) * mm, v(12.18, 6.28) * mm, v(12.25, 6.14) * mm, v(12.25, 5.97) * mm]});
            skFitSpline(sketch, "E189", {"points": [v(12.25, 5.97) * mm, v(12.25, 5.8) * mm, v(12.19, 5.66) * mm, v(12.06, 5.55) * mm]});
            skFitSpline(sketch, "E190", {"points": [v(12.06, 5.55) * mm, v(11.94, 5.44) * mm, v(11.76, 5.4) * mm, v(11.53, 5.4) * mm]});
            skLineSegment(sketch, "E191", {"start": v(8.63, 11.7) * mm, "end": v(8.63, 6.57) * mm});
            skLineSegment(sketch, "E192", {"start": v(8.63, 6.57) * mm, "end": v(11.53, 6.57) * mm});
            skFitSpline(sketch, "E193", {"points": [v(8.08, 5.4) * mm, v(7.77, 5.4) * mm, v(7.54, 5.46) * mm, v(7.4, 5.6) * mm]});
            skFitSpline(sketch, "E194", {"points": [v(7.4, 5.6) * mm, v(7.27, 5.74) * mm, v(7.2, 5.96) * mm, v(7.2, 6.27) * mm]});
            skLineSegment(sketch, "E195", {"start": v(11.53, 5.4) * mm, "end": v(8.08, 5.4) * mm});
            skLineSegment(sketch, "E196", {"start": v(8.08, 5.4) * mm, "end": v(11.53, 5.4) * mm});
            skFitSpline(sketch, "E197", {"points": [v(7.2, 11.7) * mm, v(7.2, 11.99) * mm, v(7.27, 12.2) * mm, v(7.4, 12.35) * mm]});
            skFitSpline(sketch, "E198", {"points": [v(7.4, 12.35) * mm, v(7.53, 12.5) * mm, v(7.7, 12.57) * mm, v(7.91, 12.57) * mm]});
            skFitSpline(sketch, "E199", {"points": [v(7.91, 12.57) * mm, v(8.13, 12.57) * mm, v(8.3, 12.5) * mm, v(8.43, 12.35) * mm]});
            skFitSpline(sketch, "E200", {"points": [v(8.43, 12.35) * mm, v(8.57, 12.2) * mm, v(8.63, 12) * mm, v(8.63, 11.7) * mm]});
            skLineSegment(sketch, "E201", {"start": v(7.2, 6.27) * mm, "end": v(7.2, 11.7) * mm});
            skLineSegment(sketch, "E202", {"start": v(7.2, 11.7) * mm, "end": v(7.2, 6.27) * mm});
            skFitSpline(sketch, "E203", {"points": [v(14.47, 9.49) * mm, v(14.8, 9.56) * mm, v(15.08, 9.62) * mm, v(15.32, 9.68) * mm, v(14.47, 9.49) * mm]});
            skFitSpline(sketch, "E204", {"points": [v(16.33, 8.7) * mm, v(16.31, 9.05) * mm, v(16.24, 9.3) * mm, v(16.12, 9.46) * mm], "construction": true});
            skFitSpline(sketch, "E205", {"points": [v(16.12, 9.46) * mm, v(16, 9.63) * mm, v(15.74, 9.7) * mm, v(15.35, 9.7) * mm], "construction": true});
            skFitSpline(sketch, "E206", {"points": [v(15.35, 9.7) * mm, v(15.02, 9.7) * mm, v(14.77, 9.66) * mm, v(14.6, 9.57) * mm], "construction": true});
            skFitSpline(sketch, "E207", {"points": [v(14.6, 9.57) * mm, v(14.43, 9.47) * mm, v(14.28, 9.34) * mm, v(14.16, 9.15) * mm], "construction": true});
            skFitSpline(sketch, "E208", {"points": [v(14.16, 9.15) * mm, v(14.04, 8.96) * mm, v(13.96, 8.84) * mm, v(13.9, 8.78) * mm], "construction": true});
            skFitSpline(sketch, "E209", {"points": [v(13.9, 8.78) * mm, v(13.86, 8.72) * mm, v(13.75, 8.7) * mm, v(13.59, 8.7) * mm], "construction": true});
            skFitSpline(sketch, "E210", {"points": [v(13.59, 8.7) * mm, v(13.44, 8.7) * mm, v(13.31, 8.74) * mm, v(13.2, 8.83) * mm], "construction": true});
            skFitSpline(sketch, "E211", {"points": [v(13.2, 8.83) * mm, v(13.1, 8.93) * mm, v(13.04, 9.05) * mm, v(13.04, 9.2) * mm, v(13.2, 8.83) * mm]});
            skFitSpline(sketch, "E212", {"points": [v(13.04, 9.2) * mm, v(13.04, 9.43) * mm, v(13.13, 9.65) * mm, v(13.3, 9.87) * mm], "construction": true});
            skFitSpline(sketch, "E213", {"points": [v(13.3, 9.87) * mm, v(13.45, 10.09) * mm, v(13.7, 10.27) * mm, v(14.06, 10.4) * mm], "construction": true});
            skFitSpline(sketch, "E214", {"points": [v(14.06, 10.4) * mm, v(14.4, 10.55) * mm, v(14.83, 10.62) * mm, v(15.35, 10.62) * mm], "construction": true});
            skFitSpline(sketch, "E215", {"points": [v(15.35, 10.62) * mm, v(15.93, 10.62) * mm, v(16.38, 10.55) * mm, v(16.71, 10.42) * mm], "construction": true});
            skFitSpline(sketch, "E216", {"points": [v(16.71, 10.42) * mm, v(17.04, 10.28) * mm, v(17.28, 10.07) * mm, v(17.41, 9.77) * mm], "construction": true});
            skFitSpline(sketch, "E217", {"points": [v(17.41, 9.77) * mm, v(17.55, 9.47) * mm, v(17.62, 9.08) * mm, v(17.62, 8.6) * mm], "construction": true});
            skFitSpline(sketch, "E218", {"points": [v(17.62, 8.6) * mm, v(17.62, 8.29) * mm, v(17.62, 8.03) * mm, v(17.61, 7.81) * mm], "construction": true});
            skFitSpline(sketch, "E219", {"points": [v(17.61, 7.81) * mm, v(17.61, 7.6) * mm, v(17.6, 7.36) * mm, v(17.6, 7.1) * mm], "construction": true});
            skFitSpline(sketch, "E220", {"points": [v(17.6, 7.1) * mm, v(17.6, 6.85) * mm, v(17.65, 6.6) * mm, v(17.73, 6.32) * mm], "construction": true});
            skFitSpline(sketch, "E221", {"points": [v(17.73, 6.32) * mm, v(17.81, 6.05) * mm, v(17.85, 5.88) * mm, v(17.85, 5.8) * mm], "construction": true});
            skFitSpline(sketch, "E222", {"points": [v(17.85, 5.8) * mm, v(17.85, 5.67) * mm, v(17.79, 5.55) * mm, v(17.66, 5.44) * mm], "construction": true});
            skFitSpline(sketch, "E223", {"points": [v(17.66, 5.44) * mm, v(17.54, 5.33) * mm, v(17.4, 5.27) * mm, v(17.23, 5.27) * mm], "construction": true});
            skFitSpline(sketch, "E224", {"points": [v(17.23, 5.27) * mm, v(17.1, 5.27) * mm, v(16.96, 5.33) * mm, v(16.83, 5.46) * mm], "construction": true});
            skFitSpline(sketch, "E225", {"points": [v(16.83, 5.46) * mm, v(16.7, 5.59) * mm, v(16.56, 5.77) * mm, v(16.41, 6.01) * mm, v(16.83, 5.46) * mm]});
            skFitSpline(sketch, "E226", {"points": [v(16.33, 7.91) * mm, v(16.13, 7.84) * mm, v(15.85, 7.77) * mm, v(15.49, 7.69) * mm]});
            skFitSpline(sketch, "E227", {"points": [v(15.53, 7.7) * mm, v(15.16, 7.62) * mm, v(14.9, 7.56) * mm, v(14.77, 7.52) * mm]});
            skFitSpline(sketch, "E228", {"points": [v(14.72, 7.52) * mm, v(14.58, 7.48) * mm, v(14.45, 7.4) * mm, v(14.32, 7.3) * mm]});
            skFitSpline(sketch, "E229", {"points": [v(14.32, 7.3) * mm, v(14.2, 7.2) * mm, v(14.13, 7.04) * mm, v(14.13, 6.85) * mm]});
            skFitSpline(sketch, "E230", {"points": [v(14.13, 6.85) * mm, v(14.13, 6.65) * mm, v(14.2, 6.48) * mm, v(14.35, 6.34) * mm]});
            skFitSpline(sketch, "E231", {"points": [v(14.35, 6.34) * mm, v(14.5, 6.2) * mm, v(14.7, 6.13) * mm, v(14.95, 6.13) * mm]});
            skFitSpline(sketch, "E232", {"points": [v(14.95, 6.13) * mm, v(15.2, 6.13) * mm, v(15.45, 6.19) * mm, v(15.67, 6.3) * mm]});
            skFitSpline(sketch, "E233", {"points": [v(15.67, 6.3) * mm, v(15.88, 6.42) * mm, v(16.05, 6.56) * mm, v(16.15, 6.74) * mm]});
            skFitSpline(sketch, "E234", {"points": [v(16.15, 6.74) * mm, v(16.27, 6.94) * mm, v(16.33, 7.27) * mm, v(16.33, 7.73) * mm]});
            skFitSpline(sketch, "E235", {"points": [v(20.03, 9.8) * mm, v(20.28, 10.07) * mm, v(20.53, 10.26) * mm, v(20.79, 10.4) * mm]});
            skFitSpline(sketch, "E236", {"points": [v(20.79, 10.4) * mm, v(21.04, 10.53) * mm, v(21.36, 10.6) * mm, v(21.74, 10.6) * mm]});
            skFitSpline(sketch, "E237", {"points": [v(21.74, 10.6) * mm, v(22.18, 10.6) * mm, v(22.56, 10.5) * mm, v(22.89, 10.3) * mm]});
            skFitSpline(sketch, "E238", {"points": [v(22.89, 10.3) * mm, v(23.22, 10.09) * mm, v(23.47, 9.79) * mm, v(23.65, 9.4) * mm]});
            skFitSpline(sketch, "E239", {"points": [v(23.65, 9.4) * mm, v(23.83, 9) * mm, v(23.92, 8.53) * mm, v(23.92, 8) * mm]});
            skFitSpline(sketch, "E240", {"points": [v(23.92, 8) * mm, v(23.92, 7.6) * mm, v(23.87, 7.23) * mm, v(23.77, 6.9) * mm]});
            skFitSpline(sketch, "E241", {"points": [v(23.77, 6.9) * mm, v(23.67, 6.57) * mm, v(23.53, 6.28) * mm, v(23.33, 6.04) * mm]});
            skFitSpline(sketch, "E242", {"points": [v(23.33, 6.04) * mm, v(23.14, 5.8) * mm, v(22.9, 5.6) * mm, v(22.63, 5.47) * mm]});
            skFitSpline(sketch, "E243", {"points": [v(22.63, 5.47) * mm, v(22.36, 5.34) * mm, v(22.06, 5.27) * mm, v(21.73, 5.27) * mm]});
            skFitSpline(sketch, "E244", {"points": [v(21.73, 5.27) * mm, v(21.52, 5.27) * mm, v(21.33, 5.3) * mm, v(21.16, 5.34) * mm]});
            skFitSpline(sketch, "E245", {"points": [v(21.16, 5.34) * mm, v(20.98, 5.4) * mm, v(20.83, 5.45) * mm, v(20.7, 5.53) * mm]});
            skFitSpline(sketch, "E246", {"points": [v(20.7, 5.53) * mm, v(20.58, 5.61) * mm, v(20.47, 5.7) * mm, v(20.38, 5.78) * mm]});
            skFitSpline(sketch, "E247", {"points": [v(20.38, 5.78) * mm, v(20.3, 5.86) * mm, v(20.18, 5.98) * mm, v(20.03, 6.15) * mm]});
            skLineSegment(sketch, "E248", {"start": v(20.03, 11.82) * mm, "end": v(20.03, 9.8) * mm});
            skLineSegment(sketch, "E249", {"start": v(20.03, 9.8) * mm, "end": v(20.03, 11.82) * mm});
            skFitSpline(sketch, "E250", {"points": [v(20.03, 6.02) * mm, v(20.03, 5.77) * mm, v(19.97, 5.59) * mm, v(19.85, 5.46) * mm]});
            skFitSpline(sketch, "E251", {"points": [v(19.85, 5.46) * mm, v(19.74, 5.33) * mm, v(19.58, 5.27) * mm, v(19.4, 5.27) * mm]});
            skFitSpline(sketch, "E252", {"points": [v(19.4, 5.27) * mm, v(19.22, 5.27) * mm, v(19.07, 5.33) * mm, v(18.96, 5.46) * mm]});
            skFitSpline(sketch, "E253", {"points": [v(18.96, 5.46) * mm, v(18.85, 5.59) * mm, v(18.8, 5.77) * mm, v(18.8, 6.02) * mm]});
            skLineSegment(sketch, "E254", {"start": v(20.03, 6.15) * mm, "end": v(20.03, 6.02) * mm});
            skLineSegment(sketch, "E255", {"start": v(20.03, 6.02) * mm, "end": v(20.03, 6.15) * mm});
            skFitSpline(sketch, "E256", {"points": [v(18.8, 11.76) * mm, v(18.8, 12.02) * mm, v(18.84, 12.23) * mm, v(18.95, 12.36) * mm]});
            skFitSpline(sketch, "E257", {"points": [v(18.95, 12.36) * mm, v(19.06, 12.5) * mm, v(19.2, 12.57) * mm, v(19.4, 12.57) * mm]});
            skFitSpline(sketch, "E258", {"points": [v(19.4, 12.57) * mm, v(19.6, 12.57) * mm, v(19.76, 12.5) * mm, v(19.87, 12.37) * mm]});
            skFitSpline(sketch, "E259", {"points": [v(19.87, 12.37) * mm, v(19.98, 12.24) * mm, v(20.03, 12.06) * mm, v(20.03, 11.82) * mm]});
            skLineSegment(sketch, "E260", {"start": v(18.8, 6.02) * mm, "end": v(18.8, 11.76) * mm});
            skLineSegment(sketch, "E261", {"start": v(18.8, 11.76) * mm, "end": v(18.8, 6.02) * mm});
            skFitSpline(sketch, "E262", {"points": [v(20.1, 7.91) * mm, v(20.1, 7.39) * mm, v(20.21, 6.99) * mm, v(20.45, 6.7) * mm]});
            skFitSpline(sketch, "E263", {"points": [v(20.45, 6.7) * mm, v(20.7, 6.43) * mm, v(21, 6.29) * mm, v(21.4, 6.29) * mm]});
            skFitSpline(sketch, "E264", {"points": [v(21.4, 6.29) * mm, v(21.72, 6.29) * mm, v(22, 6.43) * mm, v(22.25, 6.72) * mm]});
            skFitSpline(sketch, "E265", {"points": [v(22.25, 6.72) * mm, v(22.49, 7) * mm, v(22.6, 7.42) * mm, v(22.6, 7.95) * mm]});
            skFitSpline(sketch, "E266", {"points": [v(22.6, 7.95) * mm, v(22.6, 8.3) * mm, v(22.56, 8.6) * mm, v(22.46, 8.85) * mm]});
            skFitSpline(sketch, "E267", {"points": [v(22.46, 8.85) * mm, v(22.36, 9.1) * mm, v(22.22, 9.29) * mm, v(22.03, 9.43) * mm]});
            skFitSpline(sketch, "E268", {"points": [v(22.03, 9.43) * mm, v(21.85, 9.56) * mm, v(21.64, 9.63) * mm, v(21.4, 9.63) * mm]});
            skFitSpline(sketch, "E269", {"points": [v(21.4, 9.63) * mm, v(21.14, 9.63) * mm, v(20.92, 9.56) * mm, v(20.72, 9.43) * mm]});
            skFitSpline(sketch, "E270", {"points": [v(20.72, 9.43) * mm, v(20.53, 9.29) * mm, v(20.38, 9.1) * mm, v(20.26, 8.83) * mm]});
            skFitSpline(sketch, "E271", {"points": [v(20.26, 8.83) * mm, v(20.15, 8.58) * mm, v(20.1, 8.27) * mm, v(20.1, 7.91) * mm]});
            skFitSpline(sketch, "E272", {"points": [v(29.2, 6.99) * mm, v(29.2, 6.63) * mm, v(29.12, 6.32) * mm, v(28.94, 6.06) * mm]});
            skFitSpline(sketch, "E273", {"points": [v(28.94, 6.06) * mm, v(28.77, 5.8) * mm, v(28.5, 5.6) * mm, v(28.16, 5.47) * mm]});
            skFitSpline(sketch, "E274", {"points": [v(28.16, 5.47) * mm, v(27.82, 5.34) * mm, v(27.4, 5.27) * mm, v(26.9, 5.27) * mm]});
            skFitSpline(sketch, "E275", {"points": [v(26.9, 5.27) * mm, v(26.43, 5.27) * mm, v(26.03, 5.34) * mm, v(25.7, 5.49) * mm]});
            skFitSpline(sketch, "E276", {"points": [v(25.7, 5.49) * mm, v(25.35, 5.63) * mm, v(25.1, 5.81) * mm, v(24.94, 6.03) * mm]});
            skFitSpline(sketch, "E277", {"points": [v(24.94, 6.03) * mm, v(24.78, 6.25) * mm, v(24.7, 6.46) * mm, v(24.7, 6.68) * mm]});
            skFitSpline(sketch, "E278", {"points": [v(24.7, 6.68) * mm, v(24.7, 6.83) * mm, v(24.76, 6.95) * mm, v(24.86, 7.05) * mm]});
            skFitSpline(sketch, "E279", {"points": [v(24.86, 7.05) * mm, v(24.96, 7.15) * mm, v(25.1, 7.2) * mm, v(25.25, 7.2) * mm]});
            skFitSpline(sketch, "E280", {"points": [v(25.25, 7.2) * mm, v(25.39, 7.2) * mm, v(25.5, 7.17) * mm, v(25.57, 7.1) * mm]});
            skFitSpline(sketch, "E281", {"points": [v(25.57, 7.1) * mm, v(25.64, 7.04) * mm, v(25.71, 6.94) * mm, v(25.78, 6.82) * mm]});
            skFitSpline(sketch, "E282", {"points": [v(25.78, 6.82) * mm, v(25.91, 6.59) * mm, v(26.07, 6.41) * mm, v(26.26, 6.3) * mm]});
            skFitSpline(sketch, "E283", {"points": [v(26.26, 6.3) * mm, v(26.45, 6.18) * mm, v(26.7, 6.12) * mm, v(27.03, 6.12) * mm]});
            skFitSpline(sketch, "E284", {"points": [v(27.03, 6.12) * mm, v(27.3, 6.12) * mm, v(27.5, 6.18) * mm, v(27.68, 6.3) * mm]});
            skFitSpline(sketch, "E285", {"points": [v(27.68, 6.3) * mm, v(27.84, 6.42) * mm, v(27.93, 6.55) * mm, v(27.93, 6.7) * mm]});
            skFitSpline(sketch, "E286", {"points": [v(27.93, 6.7) * mm, v(27.93, 6.93) * mm, v(27.84, 7.1) * mm, v(27.67, 7.2) * mm]});
            skFitSpline(sketch, "E287", {"points": [v(27.67, 7.2) * mm, v(27.5, 7.31) * mm, v(27.2, 7.41) * mm, v(26.8, 7.5) * mm]});
            skFitSpline(sketch, "E288", {"points": [v(26.8, 7.5) * mm, v(26.35, 7.62) * mm, v(25.98, 7.74) * mm, v(25.7, 7.86) * mm]});
            skFitSpline(sketch, "E289", {"points": [v(25.7, 7.86) * mm, v(25.41, 7.99) * mm, v(25.19, 8.15) * mm, v(25.02, 8.35) * mm]});
            skFitSpline(sketch, "E290", {"points": [v(25.02, 8.35) * mm, v(24.85, 8.55) * mm, v(24.76, 8.8) * mm, v(24.76, 9.1) * mm]});
            skFitSpline(sketch, "E291", {"points": [v(24.76, 9.1) * mm, v(24.76, 9.36) * mm, v(24.84, 9.6) * mm, v(25, 9.84) * mm]});
            skFitSpline(sketch, "E292", {"points": [v(25, 9.84) * mm, v(25.16, 10.08) * mm, v(25.39, 10.26) * mm, v(25.7, 10.4) * mm]});
            skFitSpline(sketch, "E293", {"points": [v(25.7, 10.4) * mm, v(26, 10.54) * mm, v(26.37, 10.61) * mm, v(26.8, 10.61) * mm]});
            skFitSpline(sketch, "E294", {"points": [v(26.8, 10.61) * mm, v(27.14, 10.61) * mm, v(27.45, 10.58) * mm, v(27.72, 10.5) * mm]});
            skFitSpline(sketch, "E295", {"points": [v(27.72, 10.5) * mm, v(28, 10.44) * mm, v(28.22, 10.34) * mm, v(28.4, 10.22) * mm]});
            skFitSpline(sketch, "E296", {"points": [v(28.4, 10.22) * mm, v(28.58, 10.1) * mm, v(28.72, 9.97) * mm, v(28.81, 9.83) * mm]});
            skFitSpline(sketch, "E297", {"points": [v(28.81, 9.83) * mm, v(28.9, 9.68) * mm, v(28.95, 9.54) * mm, v(28.95, 9.4) * mm]});
            skFitSpline(sketch, "E298", {"points": [v(28.95, 9.4) * mm, v(28.95, 9.25) * mm, v(28.9, 9.13) * mm, v(28.8, 9.03) * mm]});
            skFitSpline(sketch, "E299", {"points": [v(28.8, 9.03) * mm, v(28.7, 8.94) * mm, v(28.56, 8.89) * mm, v(28.37, 8.89) * mm]});
            skFitSpline(sketch, "E300", {"points": [v(28.37, 8.89) * mm, v(28.24, 8.89) * mm, v(28.12, 8.93) * mm, v(28.03, 9) * mm]});
            skFitSpline(sketch, "E301", {"points": [v(28.03, 9) * mm, v(27.93, 9.08) * mm, v(27.82, 9.2) * mm, v(27.7, 9.35) * mm]});
            skFitSpline(sketch, "E302", {"points": [v(27.7, 9.35) * mm, v(27.6, 9.48) * mm, v(27.49, 9.58) * mm, v(27.35, 9.66) * mm]});
            skFitSpline(sketch, "E303", {"points": [v(27.35, 9.66) * mm, v(27.22, 9.74) * mm, v(27.03, 9.78) * mm, v(26.8, 9.78) * mm]});
            skFitSpline(sketch, "E304", {"points": [v(26.8, 9.78) * mm, v(26.57, 9.78) * mm, v(26.37, 9.72) * mm, v(26.21, 9.62) * mm]});
            skFitSpline(sketch, "E305", {"points": [v(26.21, 9.62) * mm, v(26.05, 9.52) * mm, v(25.97, 9.4) * mm, v(25.97, 9.25) * mm]});
            skFitSpline(sketch, "E306", {"points": [v(25.97, 9.25) * mm, v(25.97, 9.1) * mm, v(26.03, 9) * mm, v(26.15, 8.9) * mm]});
            skFitSpline(sketch, "E307", {"points": [v(26.15, 8.9) * mm, v(26.26, 8.82) * mm, v(26.42, 8.75) * mm, v(26.61, 8.69) * mm]});
            skFitSpline(sketch, "E308", {"points": [v(26.61, 8.69) * mm, v(26.81, 8.63) * mm, v(27.08, 8.56) * mm, v(27.42, 8.48) * mm]});
            skFitSpline(sketch, "E309", {"points": [v(27.42, 8.48) * mm, v(27.83, 8.38) * mm, v(28.16, 8.26) * mm, v(28.42, 8.12) * mm]});
            skFitSpline(sketch, "E310", {"points": [v(28.42, 8.12) * mm, v(28.68, 7.98) * mm, v(28.88, 7.82) * mm, v(29, 7.63) * mm]});
            skFitSpline(sketch, "E311", {"points": [v(29, 7.63) * mm, v(29.14, 7.44) * mm, v(29.2, 7.23) * mm, v(29.2, 6.99) * mm]});
            skFitSpline(sketch, "E312", {"points": [v(-3.15, 7.4) * mm, v(-3.2, 7.4) * mm, v(-3.25, 7.4) * mm, v(-3.33, 7.4) * mm]});
            skFitSpline(sketch, "E313", {"points": [v(-3.33, 7.4) * mm, v(-3.33, 7.6) * mm, v(-3.33, 7.8) * mm, v(-3.33, 8) * mm]});
            skFitSpline(sketch, "E314", {"points": [v(-3.33, 8) * mm, v(-3.31, 8.8) * mm, v(-3.63, 9.52) * mm, v(-4.1, 10.18) * mm]});
            skFitSpline(sketch, "E315", {"points": [v(-4.1, 10.18) * mm, v(-4.72, 11.09) * mm, v(-4.8, 12.03) * mm, v(-4.22, 12.97) * mm]});
            skFitSpline(sketch, "E316", {"points": [v(-4.22, 12.97) * mm, v(-3.78, 13.7) * mm, v(-3.08, 14.12) * mm, v(-2.13, 14.1) * mm]});
            skFitSpline(sketch, "E317", {"points": [v(-2.13, 14.1) * mm, v(-1.38, 14.1) * mm, v(-0.8, 13.75) * mm, v(-0.34, 13.22) * mm]});
            skFitSpline(sketch, "E318", {"points": [v(-0.34, 13.22) * mm, v(0.42, 12.32) * mm, v(0.45, 11.05) * mm, v(-0.31, 10.11) * mm]});
            skFitSpline(sketch, "E319", {"points": [v(-0.31, 10.11) * mm, v(-0.7, 9.63) * mm, v(-0.94, 9.1) * mm, v(-1.1, 8.54) * mm]});
            skFitSpline(sketch, "E320", {"points": [v(-1.1, 8.54) * mm, v(-1.2, 8.26) * mm, v(-1.16, 7.94) * mm, v(-1.2, 7.64) * mm]});
            skFitSpline(sketch, "E321", {"points": [v(-1.2, 7.64) * mm, v(-1.2, 7.56) * mm, v(-1.2, 7.48) * mm, v(-1.2, 7.4) * mm]});
            skFitSpline(sketch, "E322", {"points": [v(-1.2, 7.4) * mm, v(-1.3, 7.4) * mm, v(-1.43, 7.4) * mm, v(-1.52, 7.4) * mm]});
            skFitSpline(sketch, "E323", {"points": [v(-1.52, 7.4) * mm, v(-2.06, 7.4) * mm, v(-2.6, 7.4) * mm, v(-3.15, 7.4) * mm]});
            skFitSpline(sketch, "E324", {"points": [v(-2.99, 5.51) * mm, v(-2.85, 5.28) * mm, v(-2.58, 5.11) * mm, v(-2.27, 5.11) * mm]});
            skFitSpline(sketch, "E325", {"points": [v(-2.27, 5.11) * mm, v(-1.85, 5.11) * mm, v(-1.51, 5.4) * mm, v(-1.47, 5.76) * mm]});
            skFitSpline(sketch, "E326", {"points": [v(-3.21, 6.9) * mm, v(-3.37, 6.88) * mm, v(-3.48, 6.76) * mm, v(-3.47, 6.65) * mm]});
            skFitSpline(sketch, "E327", {"points": [v(-3.47, 6.65) * mm, v(-3.47, 6.54) * mm, v(-3.34, 6.47) * mm, v(-3.2, 6.5) * mm]});
            skFitSpline(sketch, "E328", {"points": [v(-3.2, 6.5) * mm, v(-2.58, 6.63) * mm, v(-1.95, 6.72) * mm, v(-1.33, 6.76) * mm]});
            skFitSpline(sketch, "E329", {"points": [v(-1.33, 6.76) * mm, v(-1.18, 6.77) * mm, v(-1.04, 6.87) * mm, v(-1.04, 6.97) * mm]});
            skFitSpline(sketch, "E330", {"points": [v(-1.04, 6.97) * mm, v(-1.03, 7.08) * mm, v(-1.15, 7.16) * mm, v(-1.3, 7.15) * mm]});
            skFitSpline(sketch, "E331", {"points": [v(-1.3, 7.15) * mm, v(-1.95, 7.11) * mm, v(-2.58, 7.03) * mm, v(-3.21, 6.9) * mm]});
            skLineSegment(sketch, "E332", {"start": v(-1.47, 5.76) * mm, "end": v(-2.99, 5.51) * mm});
            skLineSegment(sketch, "E333", {"start": v(-2.99, 5.51) * mm, "end": v(-1.47, 5.76) * mm});
            skFitSpline(sketch, "E334", {"points": [v(-3.17, 6.19) * mm, v(-3.32, 6.16) * mm, v(-3.43, 6.04) * mm, v(-3.42, 5.93) * mm]});
            skFitSpline(sketch, "E335", {"points": [v(-3.42, 5.93) * mm, v(-3.4, 5.81) * mm, v(-3.29, 5.75) * mm, v(-3.15, 5.78) * mm]});
            skFitSpline(sketch, "E336", {"points": [v(-3.15, 5.78) * mm, v(-2.45, 5.94) * mm, v(-2.1, 6) * mm, v(-1.37, 6.06) * mm]});
            skFitSpline(sketch, "E337", {"points": [v(-1.37, 6.06) * mm, v(-1.23, 6.08) * mm, v(-1.1, 6.17) * mm, v(-1.1, 6.28) * mm]});
            skFitSpline(sketch, "E338", {"points": [v(-1.1, 6.28) * mm, v(-1.08, 6.39) * mm, v(-1.2, 6.47) * mm, v(-1.35, 6.46) * mm]});
            skFitSpline(sketch, "E339", {"points": [v(-1.35, 6.46) * mm, v(-2.09, 6.4) * mm, v(-2.46, 6.34) * mm, v(-3.17, 6.19) * mm]});
            skLineSegment(sketch, "E340", {"start": v(-29.21, 0) * mm, "end": v(29.21, 0) * mm, "construction": true});
            skPoint(sketch, "E341", {"position": v(0, 0) * mm});
            skFitSpline(sketch, "E342", {"points": [v(16.33, 8.7) * mm, v(16.12, 9.46) * mm, v(15.35, 9.7) * mm, v(14.6, 9.57) * mm, v(14.16, 9.15) * mm, v(13.9, 8.78) * mm, v(13.59, 8.7) * mm, v(13.2, 8.83) * mm, v(13.04, 9.2) * mm, v(13.3, 9.87) * mm, v(14.06, 10.4) * mm, v(15.35, 10.62) * mm, v(16.71, 10.42) * mm, v(17.41, 9.77) * mm, v(17.62, 8.6) * mm, v(17.61, 7.81) * mm, v(17.6, 7.1) * mm, v(17.73, 6.32) * mm, v(17.85, 5.8) * mm, v(17.66, 5.44) * mm, v(17.23, 5.27) * mm, v(16.83, 5.46) * mm, v(16.41, 6.01) * mm], "startDerivative": vector(-1.37, 18.14) * mm, "endDerivative": vector(-8.82, 13.53) * mm});
            skLineSegment(sketch, "E343", {"start": v(16.33, 7.73) * mm, "end": v(16.33, 7.91) * mm});
            skFitSpline(sketch, "E344", {"points": [v(16.33, 8.7) * mm, v(15.48, 8.47) * mm, v(14.67, 8.3) * mm, v(14.09, 8.16) * mm, v(13.38, 7.73) * mm, v(13.03, 6.87) * mm, v(13.46, 5.85) * mm, v(14.38, 5.38) * mm, v(15.56, 5.51) * mm, v(16.41, 6.01) * mm], "startDerivative": vector(-7.54, -2.24) * mm, "endDerivative": vector(6.05, 4.6) * mm});
            skLineSegment(sketch, "E345", {"start": v(14.72, 7.52) * mm, "end": v(14.77, 7.52) * mm});
            skSolve(sketch);
        }
        {
            var Q0;
            Q0=makeQuery(id+"F7.imprint","IMPRINT",FACE,{"disambiguationData":[TD([[makeQuery(id+"F7.imprint","IMPRINT",EDGE,{"derivedFrom":sQuery(id+"F7.wireOp",EDGE,"E8")}),-1.0]])]});
            var Q1;
            Q1=makeQuery(id+"F7.imprint","IMPRINT",FACE,{"disambiguationData":[TD([[makeQuery(id+"F7.imprint","IMPRINT",EDGE,{"derivedFrom":sQuery(id+"F7.wireOp",EDGE,"E47")}),-1.0]])]});
            var Q2;
            Q2=makeQuery(id+"F7.imprint","IMPRINT",FACE,{"disambiguationData":[TD([[makeQuery(id+"F7.imprint","IMPRINT",EDGE,{"derivedFrom":sQuery(id+"F7.wireOp",EDGE,"E91")}),-1.0]])]});
            var Q3;
            Q3=makeQuery(id+"F7.imprint","IMPRINT",FACE,{"disambiguationData":[TD([[makeQuery(id+"F7.imprint","IMPRINT",EDGE,{"derivedFrom":sQuery(id+"F7.wireOp",EDGE,"E119")}),-1.0]])]});
            var Q4;
            Q4=makeQuery(id+"F7.imprint","IMPRINT",FACE,{"disambiguationData":[TD([[makeQuery(id+"F7.imprint","IMPRINT",EDGE,{"derivedFrom":sQuery(id+"F7.wireOp",EDGE,"E312")}),-1.0]])]});
            var Q5;
            Q5=makeQuery(id+"F7.imprint","IMPRINT",FACE,{"disambiguationData":[TD([[makeQuery(id+"F7.imprint","IMPRINT",EDGE,{"derivedFrom":sQuery(id+"F7.wireOp",EDGE,"E326")}),1.0]])]});
            var Q6;
            Q6=makeQuery(id+"F7.imprint","IMPRINT",FACE,{"disambiguationData":[TD([[makeQuery(id+"F7.imprint","IMPRINT",EDGE,{"derivedFrom":sQuery(id+"F7.wireOp",EDGE,"E334")}),1.0]])]});
            var Q7;
            Q7=makeQuery(id+"F7.imprint","IMPRINT",FACE,{"disambiguationData":[TD([[makeQuery(id+"F7.imprint","IMPRINT",EDGE,{"derivedFrom":sQuery(id+"F7.wireOp",EDGE,"E324")}),1.0]])]});
            var Q8;
            Q8=makeQuery(id+"F7.imprint","IMPRINT",FACE,{"disambiguationData":[TD([[makeQuery(id+"F7.imprint","IMPRINT",EDGE,{"derivedFrom":sQuery(id+"F7.wireOp",EDGE,"E152")}),-1.0]])]});
            var Q9;
            Q9=makeQuery(id+"F7.imprint","IMPRINT",FACE,{"disambiguationData":[TD([[makeQuery(id+"F7.imprint","IMPRINT",EDGE,{"derivedFrom":sQuery(id+"F7.wireOp",EDGE,"E187")}),-1.0]])]});
            var Q10;
            Q10=makeQuery(id+"F7.imprint","IMPRINT",FACE,{"disambiguationData":[TD([[makeQuery(id+"F7.imprint","IMPRINT",EDGE,{"derivedFrom":sQuery(id+"F7.wireOp",EDGE,"E235")}),-1.0]])]});
            var Q11;
            Q11=makeQuery(id+"F7.imprint","IMPRINT",FACE,{"disambiguationData":[TD([[makeQuery(id+"F7.imprint","IMPRINT",EDGE,{"derivedFrom":sQuery(id+"F7.wireOp",EDGE,"E272")}),-1.0]])]});
            var Q12;
            Q12=makeQuery(id+"F7.imprint","IMPRINT",FACE,{"disambiguationData":[TD([[makeQuery(id+"F7.imprint","IMPRINT",EDGE,{"derivedFrom":sQuery(id+"F7.wireOp",EDGE,"E226")}),-1.0]])]});
            var Q13;
            Q13=makeQuery(id+"F7.imprint","IMPRINT",FACE,{"disambiguationData":[TD([[makeQuery(id+"F7.imprint","IMPRINT",EDGE,{"derivedFrom":sQuery(id+"F7.wireOp",EDGE,"E342")}),-1.0]])]});
            extrude(context, id + "F8", {"entities" : qUnion([Q0, Q1, Q2, Q3, Q4, Q5, Q6, Q7, Q8, Q9, Q10, Q11, Q12, Q13]), "operationType" : NewBodyOperationType.REMOVE, "oppositeDirection" : true, "depth" : 25.4 * mm});
        }
        {
            var Q0;
            {var subQ0=sQuery(id+"F2.wireOp",EDGE,"E6");Q0=makeQuery(id+"F8.boolean.opBoolean","SPLIT",FACE,{"disambiguationData":[TD([makeQuery(id+"F3.opExtrude","SWEPT_FACE",FACE,{"disambiguationData":[OSD([subQ0])]})])],"derivedFrom":makeQuery(id+"F3.opExtrude","CAP_FACE",FACE,{"disambiguationData":[OSD([subQ0])],"isStart":false})});}
            var sketch = newSketch(context, id + "F9", { "sketchPlane" : qUnion([Q0])});
            skText(sketch, "E346", { "text": "LASER BURN\n       TAPE", "fontName": "AllertaStencil-Regular.ttf"});
            skLineSegment(sketch, "E347", {"start": v(0, 0) * mm, "end": v(0, -2.54) * mm, "construction": true});
            const initialGuessF9  = {"E346": [-0.03175, -0.01016, 1, 0, 0.00762]};
            skSetInitialGuess(sketch, initialGuessF9);
            skSolve(sketch);
        }
        {
            var Q0;
            Q0 = qSketchRegion(id + "F9", true);
            extrude(context, id + "F10", {"entities" : qUnion([Q0]), "operationType" : NewBodyOperationType.REMOVE, "oppositeDirection" : true, "depth" : 25.4 * mm});
        }
        {
            var Q0;
            {var subQ0=sQuery(id+"F4.wireOp",EDGE,"E7");Q0=makeQuery(id+"F8.boolean.opBoolean","SPLIT",FACE,{"disambiguationData":[TD([makeQuery(id+"F8.opExtrude","SWEPT_FACE",FACE,{"disambiguationData":[OSD([sQuery(id+"F7.wireOp",EDGE,"E8")])]})])],"derivedFrom":makeQuery(id+"F5.boolean.opBoolean","COPY",FACE,{"derivedFrom":makeQuery(id+"F5.opExtrude","CAP_FACE",FACE,{"disambiguationData":[OSD([subQ0])],"isStart":false})})});}
            var sketch = newSketch(context, id + "F11", { "sketchPlane" : qUnion([Q0])});
            skLineSegment(sketch, "E348.bottom", {"start": v(-19.09, -4.35) * mm, "end": v(-18.33, -4.35) * mm});
            skLineSegment(sketch, "E348.top", {"start": v(-19.09, -9.12) * mm, "end": v(-18.33, -9.12) * mm});
            skLineSegment(sketch, "E348.left", {"start": v(-19.09, -4.35) * mm, "end": v(-19.09, -9.12) * mm});
            skLineSegment(sketch, "E348.right", {"start": v(-18.33, -4.35) * mm, "end": v(-18.33, -9.12) * mm});
            skLineSegment(sketch, "E349.bottom", {"start": v(-7.71, -6.99) * mm, "end": v(-6.95, -6.99) * mm});
            skLineSegment(sketch, "E349.top", {"start": v(-7.71, -11.77) * mm, "end": v(-6.95, -11.77) * mm});
            skLineSegment(sketch, "E349.left", {"start": v(-7.71, -6.99) * mm, "end": v(-7.71, -11.77) * mm});
            skLineSegment(sketch, "E349.right", {"start": v(-6.95, -6.99) * mm, "end": v(-6.95, -11.77) * mm});
            skLineSegment(sketch, "E350.bottom", {"start": v(21.28, -4.2) * mm, "end": v(22, -4.2) * mm});
            skLineSegment(sketch, "E350.top", {"start": v(21.28, -12.17) * mm, "end": v(22, -12.17) * mm});
            skLineSegment(sketch, "E350.left", {"start": v(21.28, -4.2) * mm, "end": v(21.28, -12.17) * mm});
            skLineSegment(sketch, "E350.right", {"start": v(22, -4.2) * mm, "end": v(22, -12.17) * mm});
            skLineSegment(sketch, "E351.bottom", {"start": v(14.88, -4.37) * mm, "end": v(15.49, -4.37) * mm});
            skLineSegment(sketch, "E351.top", {"start": v(14.88, -8.95) * mm, "end": v(15.49, -8.95) * mm});
            skLineSegment(sketch, "E351.left", {"start": v(14.88, -4.37) * mm, "end": v(14.88, -8.95) * mm});
            skLineSegment(sketch, "E351.right", {"start": v(15.49, -4.37) * mm, "end": v(15.49, -8.95) * mm});
            skSolve(sketch);
        }
        {
            var Q0;
            Q0 = qSketchRegion(id + "F11", true);
            extrude(context, id + "F12", {"entities" : qUnion([Q0]), "operationType" : NewBodyOperationType.ADD, "depth" : 1.27 * mm});
        }
        {
            var Q0;
            Q0=makeQuery(id+"F12.opExtrude","CAP_EDGE",EDGE,{"disambiguationData":[OSD([sQuery(id+"F11.wireOp",EDGE,"E348.bottom")])],"isStart":false});
            var Q1;
            Q1=makeQuery(id+"F12.opExtrude","CAP_EDGE",EDGE,{"disambiguationData":[OSD([sQuery(id+"F11.wireOp",EDGE,"E348.top")])],"isStart":false});
            var Q2;
            Q2=makeQuery(id+"F12.opExtrude","CAP_EDGE",EDGE,{"disambiguationData":[OSD([sQuery(id+"F11.wireOp",EDGE,"E349.bottom")])],"isStart":false});
            var Q3;
            Q3=makeQuery(id+"F12.opExtrude","CAP_EDGE",EDGE,{"disambiguationData":[OSD([sQuery(id+"F11.wireOp",EDGE,"E349.top")])],"isStart":false});
            var Q4;
            Q4=makeQuery(id+"F12.opExtrude","CAP_EDGE",EDGE,{"disambiguationData":[OSD([sQuery(id+"F11.wireOp",EDGE,"E351.bottom")])],"isStart":false});
            var Q5;
            Q5=makeQuery(id+"F12.opExtrude","CAP_EDGE",EDGE,{"disambiguationData":[OSD([sQuery(id+"F11.wireOp",EDGE,"E351.top")])],"isStart":false});
            var Q6;
            Q6=makeQuery(id+"F12.opExtrude","CAP_EDGE",EDGE,{"disambiguationData":[OSD([sQuery(id+"F11.wireOp",EDGE,"E350.bottom")])],"isStart":false});
            var Q7;
            Q7=makeQuery(id+"F12.opExtrude","CAP_EDGE",EDGE,{"disambiguationData":[OSD([sQuery(id+"F11.wireOp",EDGE,"E350.top")])],"isStart":false});
            chamfer(context, id + "F13", {"entities" : qUnion([Q0, Q1, Q2, Q3, Q4, Q5, Q6, Q7]), "width" : 1.02 * mm, "tangentPropagation" : true});
        }
    });
